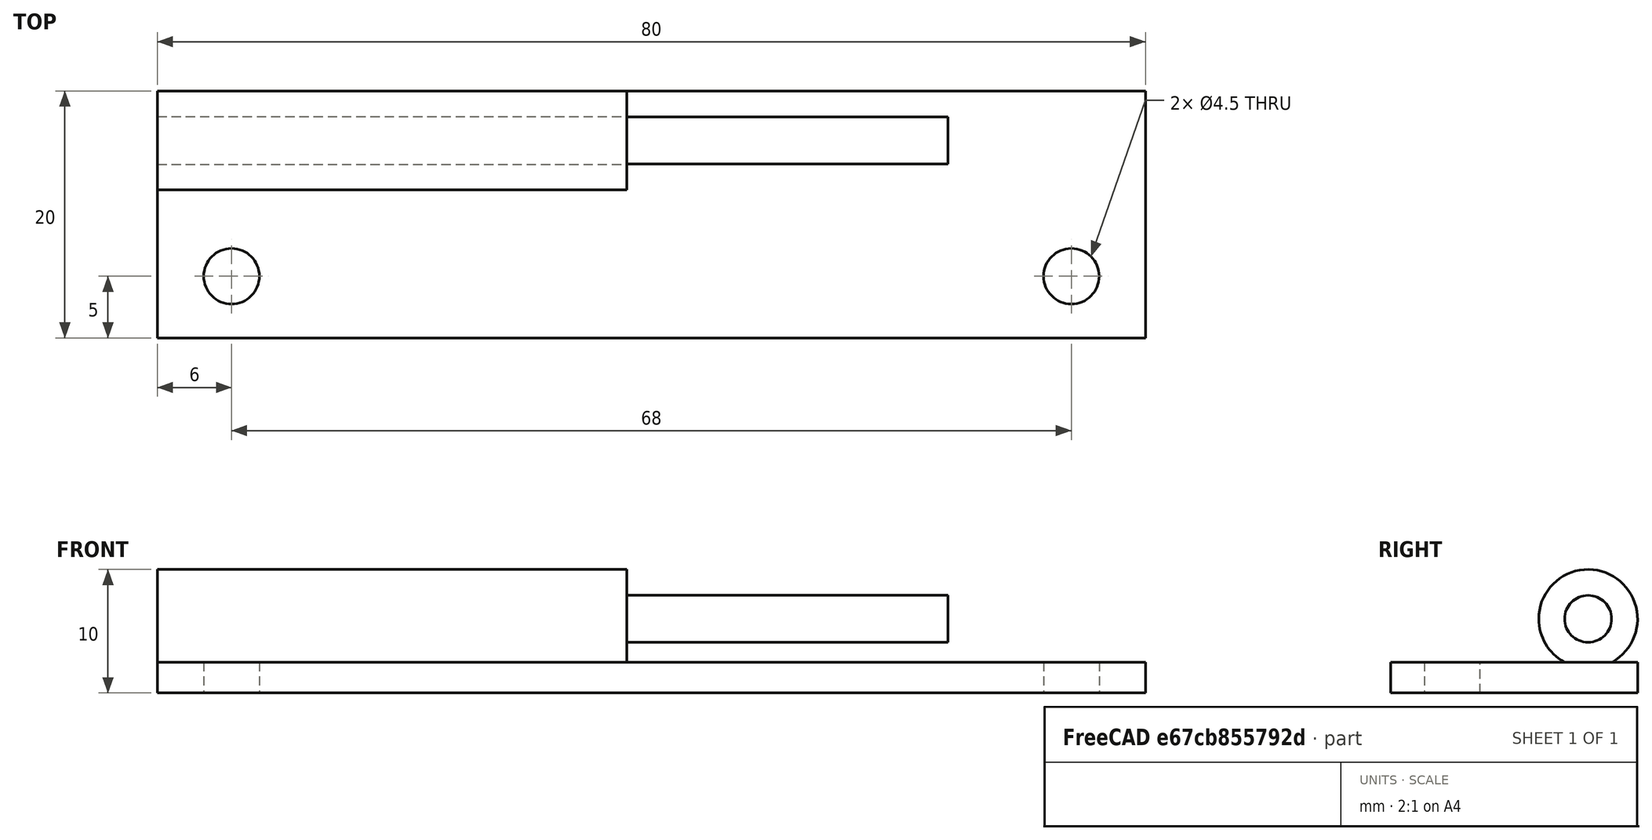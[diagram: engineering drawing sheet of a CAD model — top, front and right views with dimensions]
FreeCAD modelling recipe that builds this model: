
FCSTD DOCUMENT  (FreeCAD 0.21R33668 +26 (Git))
Label: 1-folding-hinge-pin
License: All rights reserved
LicenseURL: http://en.wikipedia.org/wiki/All_rights_reserved
objects: PartDesign::AdditiveCylinder×2, PartDesign::SubtractiveCylinder×2, PartDesign::AdditiveBox×1, PartDesign::Body×1
note: 11 computed .brp shape members not serialized (recipe doc carries the construction recipe); baked Part::Feature solids carry a one-line shape summary decoded from their .brp

FEATURE [PartDesign::AdditiveBox] Box
  AttacherType = Attacher::AttachEngine3D
  Height = 2.5
  Length = 80
  Width = 20
FEATURE [PartDesign::AdditiveCylinder] Cylinder
  Angle = 360
  AttacherType = Attacher::AttachEngine3D
  AttachmentOffset = pos=(-16,6,-38) rot=(0,0,1;0rad)
  BaseFeature = -> Box
  FirstAngle = 0
  Height = 38
  MapMode = 5
  Placement = pos=(38,16,6) rot=(0.57735,-0.57735,-0.57735;2.0944rad)
  Radius = 4
  SecondAngle = 0
  Support = -> [Box]
FEATURE [PartDesign::AdditiveCylinder] Cylinder001  label="pin"
  Angle = 360
  AttacherType = Attacher::AttachEngine3D
  AttachmentOffset = pos=(0,0,-64) rot=(0,0,1;0rad)
  BaseFeature = -> Cylinder
  FirstAngle = 0
  Height = 30
  MapMode = 5
  Placement = pos=(64,16,6) rot=(0.57735,-0.57735,-0.57735;2.0944rad)
  Radius = 1.9
  SecondAngle = 0
  Support = -> [Cylinder]
FEATURE [PartDesign::SubtractiveCylinder] Cylinder002  label="mp1"
  Angle = 360
  AttacherType = Attacher::AttachEngine3D
  AttachmentOffset = pos=(-11,-10,-2.5) rot=(0,0,1;0rad)
  BaseFeature = -> Cylinder001
  FirstAngle = 0
  Height = 2.5
  MapMode = 5
  Placement = pos=(74,5,6.7e-15) rot=(0,0,1;1.5708rad)
  Radius = 2.25
  SecondAngle = 0
  Support = -> [Cylinder001]
FEATURE [PartDesign::SubtractiveCylinder] Cylinder003  label="mp2"
  Angle = 360
  AttacherType = Attacher::AttachEngine3D
  AttachmentOffset = pos=(0,68,-2.5) rot=(0,0,1;0rad)
  BaseFeature = -> Cylinder002
  FirstAngle = 0
  Height = 2.5
  MapMode = 5
  Placement = pos=(6,5,6.7e-15) rot=(0,0,1;1.5708rad)
  Radius = 2.25
  SecondAngle = 0
  Support = -> [Cylinder002]
FEATURE [PartDesign::Body] Body
  Group = -> [Box,Cylinder,Cylinder001,Cylinder002,Cylinder003]
  Origin = -> Origin
  Tip = -> Cylinder003
